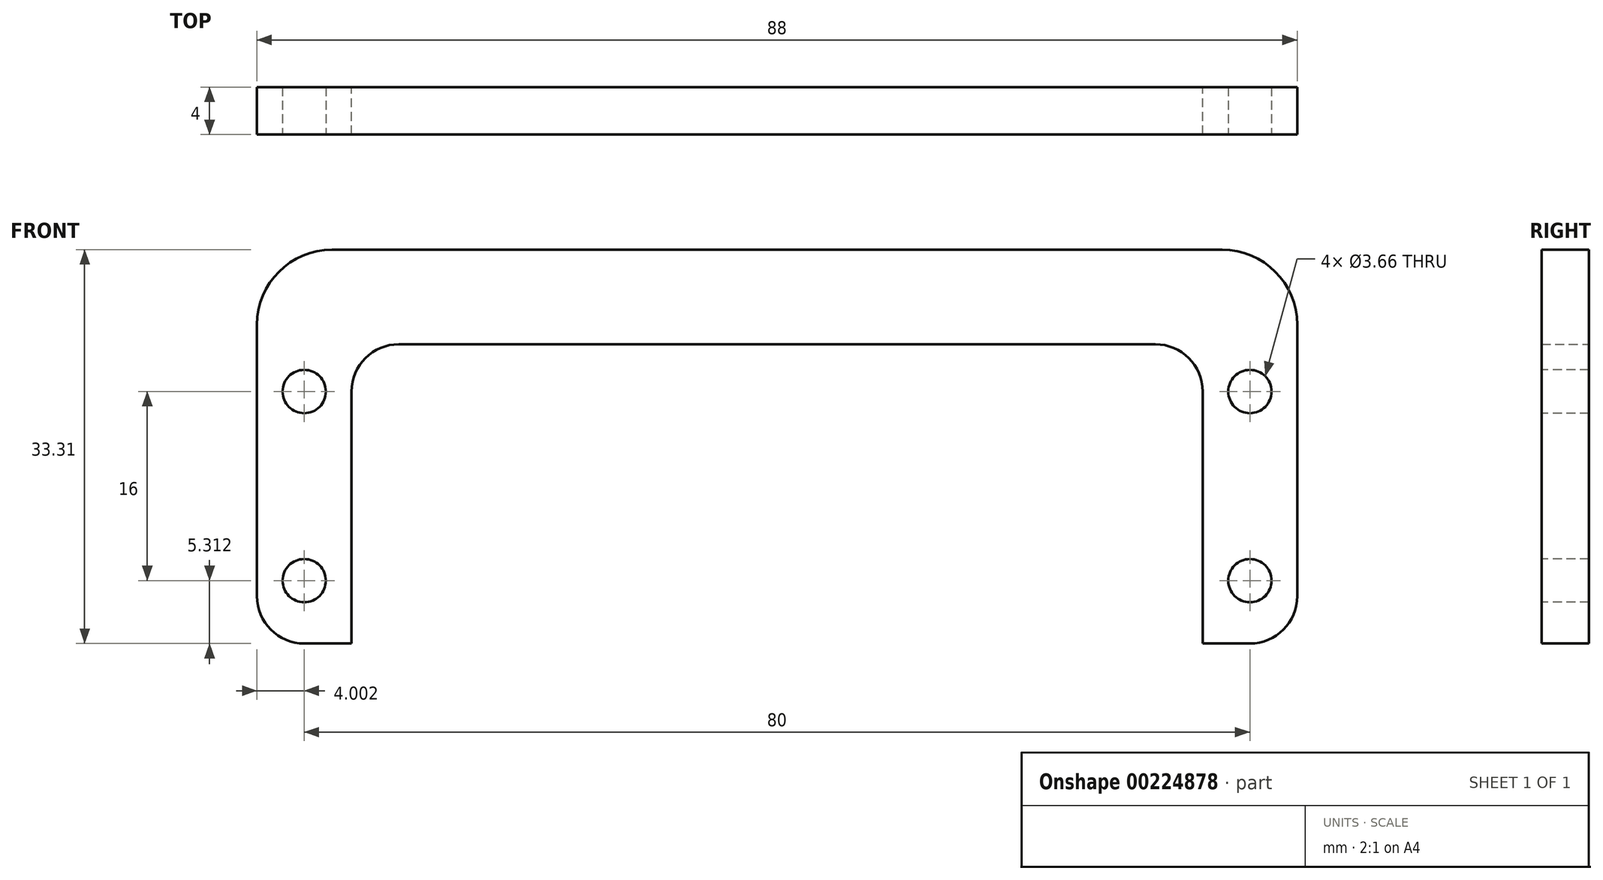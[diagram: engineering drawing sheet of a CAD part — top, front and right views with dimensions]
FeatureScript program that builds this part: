
annotation { "Feature Type Name" : "Feature", "Feature Type Description" : "" }
export const myFeature = defineFeature(function(context is Context, id is Id, definition is map)
    precondition{}
    {
        {
            var Q0;
            Q0=qCreatedBy(makeId("Front.planeOp"),FACE);
            var sketch = newSketch(context, id + "F0", { "sketchPlane" : qUnion([Q0])});
            skLineSegment(sketch, "E0", {"start": v(-36.38, -10) * mm, "end": v(-36.38, 11.31) * mm});
            skLineSegment(sketch, "E1", {"start": v(-32.38, 15.31) * mm, "end": v(31.62, 15.31) * mm});
            skLineSegment(sketch, "E2", {"start": v(35.62, 11.31) * mm, "end": v(35.62, -10) * mm});
            skLineSegment(sketch, "E3", {"start": v(35.62, -10) * mm, "end": v(39.62, -10) * mm});
            skLineSegment(sketch, "E4", {"start": v(43.62, -6) * mm, "end": v(43.62, 16.96) * mm});
            skLineSegment(sketch, "E5", {"start": v(37.27, 23.31) * mm, "end": v(-38.03, 23.31) * mm});
            skLineSegment(sketch, "E6", {"start": v(-44.38, 16.96) * mm, "end": v(-44.38, -6) * mm});
            skLineSegment(sketch, "E7", {"start": v(-40.38, -10) * mm, "end": v(-36.38, -10) * mm});
            skPoint(sketch, "E8.visualSharp", {"position": v(-44.38, 23.31) * mm});
            skArc(sketch, "E8.filletArc", {"start": v(-38.03, 23.31) * mm, "mid": v(-42.52, 21.45) * mm, "end": v(-44.38, 16.96) * mm});
            skPoint(sketch, "E9.visualSharp", {"position": v(-36.38, 15.31) * mm});
            skArc(sketch, "E9.filletArc", {"start": v(-32.38, 15.31) * mm, "mid": v(-35.2, 14.14) * mm, "end": v(-36.38, 11.31) * mm});
            skPoint(sketch, "E10.visualSharp", {"position": v(35.62, 15.31) * mm});
            skArc(sketch, "E10.filletArc", {"start": v(35.62, 11.31) * mm, "mid": v(34.45, 14.14) * mm, "end": v(31.62, 15.31) * mm});
            skPoint(sketch, "E11.visualSharp", {"position": v(43.62, 23.31) * mm});
            skArc(sketch, "E11.filletArc", {"start": v(43.62, 16.96) * mm, "mid": v(41.76, 21.45) * mm, "end": v(37.27, 23.31) * mm});
            skPoint(sketch, "E12.visualSharp", {"position": v(43.62, -10) * mm});
            skArc(sketch, "E12.filletArc", {"start": v(39.62, -10) * mm, "mid": v(42.45, -8.83) * mm, "end": v(43.62, -6) * mm});
            skPoint(sketch, "E13.visualSharp", {"position": v(-44.38, -10) * mm});
            skArc(sketch, "E13.filletArc", {"start": v(-44.38, -6) * mm, "mid": v(-43.2, -8.83) * mm, "end": v(-40.38, -10) * mm});
            skSolve(sketch);
        }
        {
            var Q0;
            Q0=makeQuery(id+"F0.imprint","IMPRINT",FACE,{"disambiguationData":[TD([[makeQuery(id+"F0.imprint","IMPRINT",EDGE,{"derivedFrom":sQuery(id+"F0.wireOp",EDGE,"E0")}),1.0]])]});
            extrude(context, id + "F1", {"entities" : qUnion([Q0]), "depth" : 4 * mm});
        }
        {
            var Q0;
            Q0=makeQuery(id+"F1.opExtrude","CAP_FACE",FACE,{"disambiguationData":[OSD([sQuery(id+"F0.wireOp",EDGE,"E0"),sQuery(id+"F0.wireOp",EDGE,"E1"),sQuery(id+"F0.wireOp",EDGE,"E2"),sQuery(id+"F0.wireOp",EDGE,"E3"),sQuery(id+"F0.wireOp",EDGE,"E4"),sQuery(id+"F0.wireOp",EDGE,"E5"),sQuery(id+"F0.wireOp",EDGE,"E6"),sQuery(id+"F0.wireOp",EDGE,"E7"),sQuery(id+"F0.wireOp",EDGE,"E8.filletArc"),sQuery(id+"F0.wireOp",EDGE,"E9.filletArc"),sQuery(id+"F0.wireOp",EDGE,"E10.filletArc"),sQuery(id+"F0.wireOp",EDGE,"E11.filletArc"),sQuery(id+"F0.wireOp",EDGE,"E12.filletArc"),sQuery(id+"F0.wireOp",EDGE,"E13.filletArc")])],"isStart":false});
            var sketch = newSketch(context, id + "F2", { "sketchPlane" : qUnion([Q0])});
            skPoint(sketch, "E14", {"position": v(-40.38, 11.31) * mm});
            skPoint(sketch, "E15", {"position": v(-40.38, -4.69) * mm});
            skPoint(sketch, "E16", {"position": v(39.62, 11.31) * mm});
            skPoint(sketch, "E17", {"position": v(39.62, -4.69) * mm});
            skSolve(sketch);
        }
        {
            var Q0;
            Q0=sQuery(id+"F2.wireOp",VERTEX,"E14");
            var Q1;
            Q1=sQuery(id+"F2.wireOp",VERTEX,"E15");
            var Q2;
            Q2=sQuery(id+"F2.wireOp",VERTEX,"E16");
            var Q3;
            Q3=sQuery(id+"F2.wireOp",VERTEX,"E17");
            var Q4;
            Q4=makeQuery(id+"F1.opExtrude","SWEPT_BODY",BODY,{"disambiguationData":[OSD([sQuery(id+"F0.wireOp",EDGE,"E0"),sQuery(id+"F0.wireOp",EDGE,"E1"),sQuery(id+"F0.wireOp",EDGE,"E2"),sQuery(id+"F0.wireOp",EDGE,"E3"),sQuery(id+"F0.wireOp",EDGE,"E4"),sQuery(id+"F0.wireOp",EDGE,"E5"),sQuery(id+"F0.wireOp",EDGE,"E6"),sQuery(id+"F0.wireOp",EDGE,"E7"),sQuery(id+"F0.wireOp",EDGE,"E8.filletArc"),sQuery(id+"F0.wireOp",EDGE,"E9.filletArc"),sQuery(id+"F0.wireOp",EDGE,"E10.filletArc"),sQuery(id+"F0.wireOp",EDGE,"E11.filletArc"),sQuery(id+"F0.wireOp",EDGE,"E12.filletArc"),sQuery(id+"F0.wireOp",EDGE,"E13.filletArc")])]});
            hole(context, id + "F3", {"style" : HoleStyle.SIMPLE, "endStyle" : HoleEndStyle.THROUGH, "standardTappedOrClearance" : lookupTablePath({ "standard" : "ANSI", "fit" : "Close", "size" : "#6", "type" : "Clearance" }), "standardBlindInLast" : lookupTablePath({ "fit" : "Close", "standard" : "ANSI", "size" : "#6", "type" : "Clearance" }), "holeDiameter" : 3.66 * mm, "locations" : qUnion([Q0, Q1, Q2, Q3]), "scope" : qUnion([Q4]), "isTappedThrough" : true});
        }
    });
